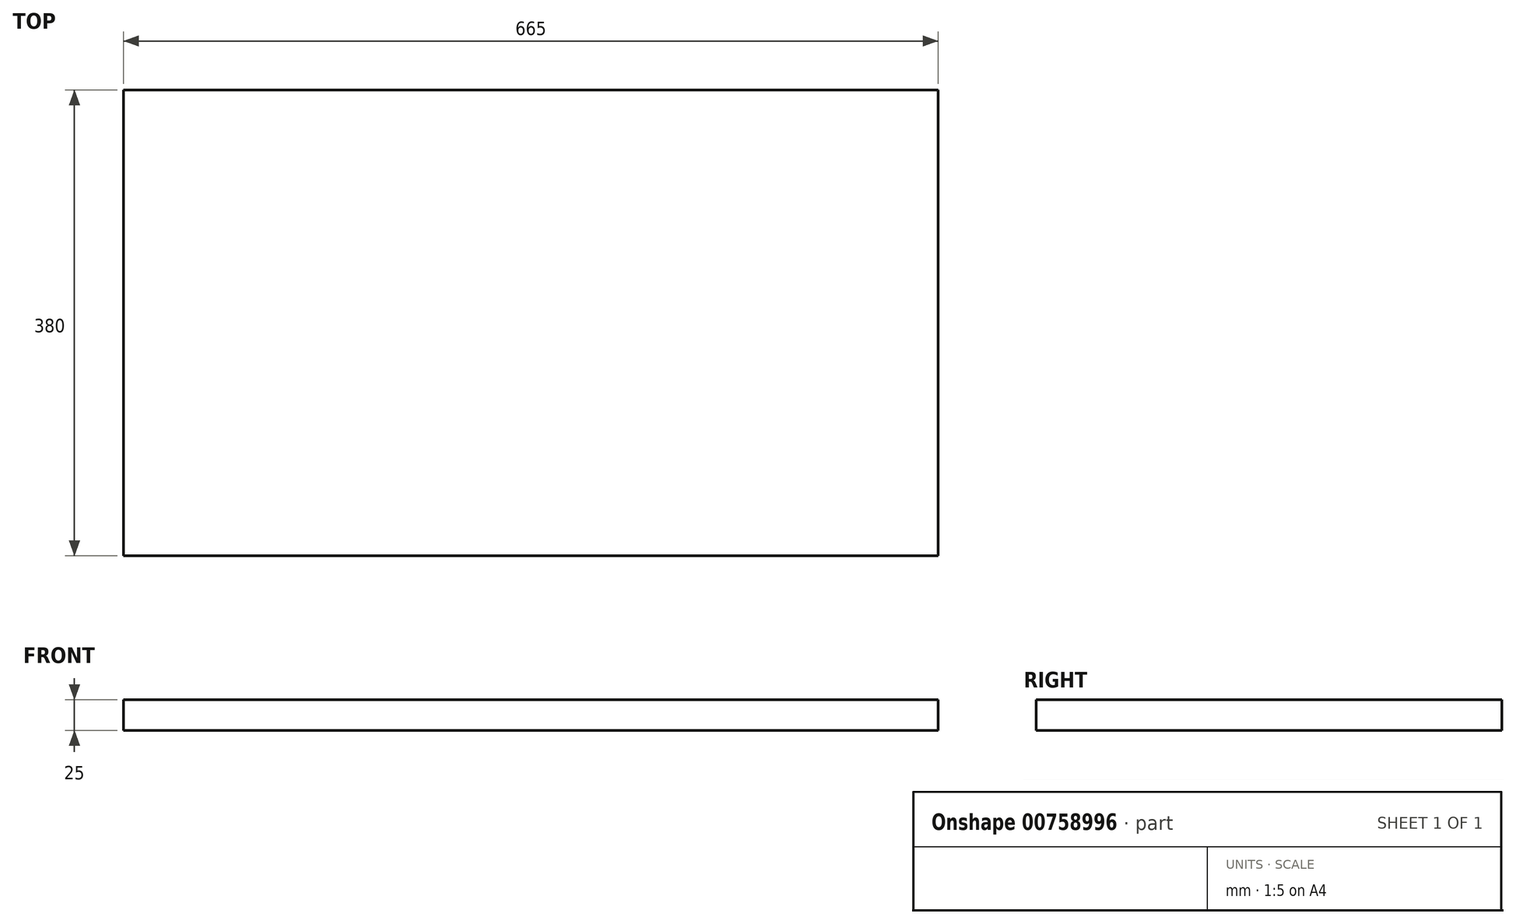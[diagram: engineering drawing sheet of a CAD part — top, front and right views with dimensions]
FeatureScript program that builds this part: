
annotation { "Feature Type Name" : "Feature", "Feature Type Description" : "" }
export const myFeature = defineFeature(function(context is Context, id is Id, definition is map)
    precondition{}
    {
        {
            var Q0;
            Q0=qCreatedBy(makeId("Top.planeOp"),FACE);
            var sketch = newSketch(context, id + "F0", { "sketchPlane" : qUnion([Q0])});
            skLineSegment(sketch, "E0.bottom", {"start": v(332.5, -190) * mm, "end": v(-332.5, -190) * mm});
            skLineSegment(sketch, "E0.top", {"start": v(332.5, 190) * mm, "end": v(-332.5, 190) * mm});
            skLineSegment(sketch, "E0.left", {"start": v(332.5, -190) * mm, "end": v(332.5, 190) * mm});
            skLineSegment(sketch, "E0.right", {"start": v(-332.5, -190) * mm, "end": v(-332.5, 190) * mm});
            skPoint(sketch, "E0.middle", {"position": v(0, 0) * mm});
            skSolve(sketch);
        }
        {
            var Q0;
            Q0 = qSketchRegion(id + "F0", true);
            extrude(context, id + "F1", {"entities" : qUnion([Q0]), "oppositeDirection" : true, "depth" : 25 * mm, "offsetDistance" : 25 * mm});
        }
    });
